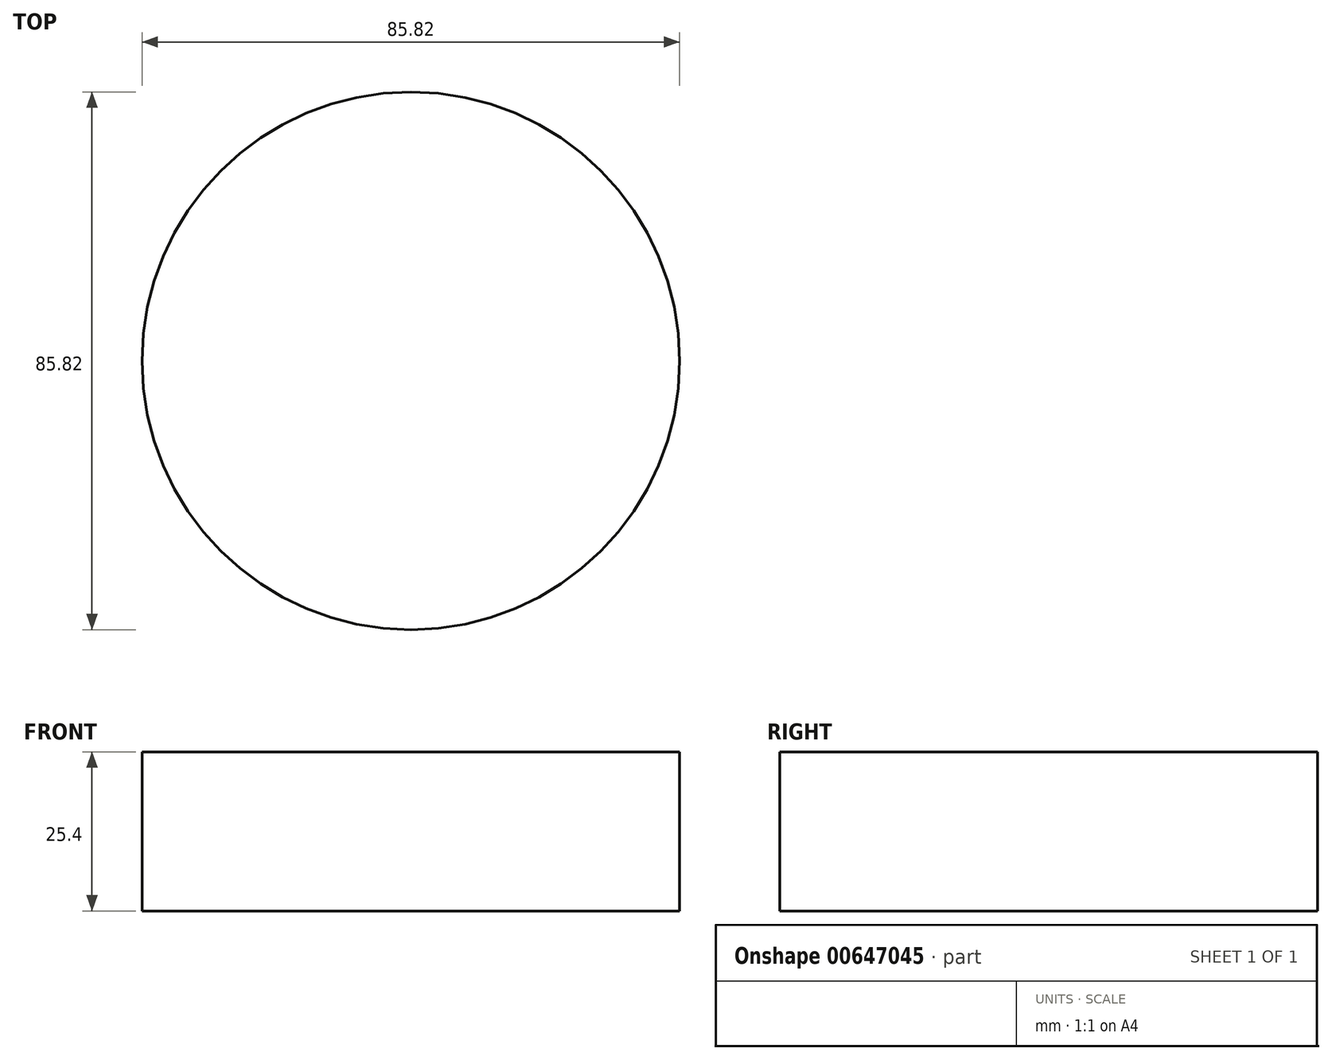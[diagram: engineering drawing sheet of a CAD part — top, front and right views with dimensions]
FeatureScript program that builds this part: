
annotation { "Feature Type Name" : "Feature", "Feature Type Description" : "" }
export const myFeature = defineFeature(function(context is Context, id is Id, definition is map)
    precondition{}
    {
        {
            var Q0;
            Q0=qCreatedBy(makeId("Top.planeOp"),FACE);
            var sketch = newSketch(context, id + "F0", { "sketchPlane" : qUnion([Q0])});
            skCircle(sketch, "E0", {"center": v(0, 0) * mm, "radius": 42.91 * mm});
            skSolve(sketch);
        }
        {
            var Q0;
            Q0 = qSketchRegion(id + "F0", true);
            extrude(context, id + "F1", {"entities" : qUnion([Q0]), "depth" : 25.4 * mm, "offsetDistance" : 25.4 * mm});
        }
    });
